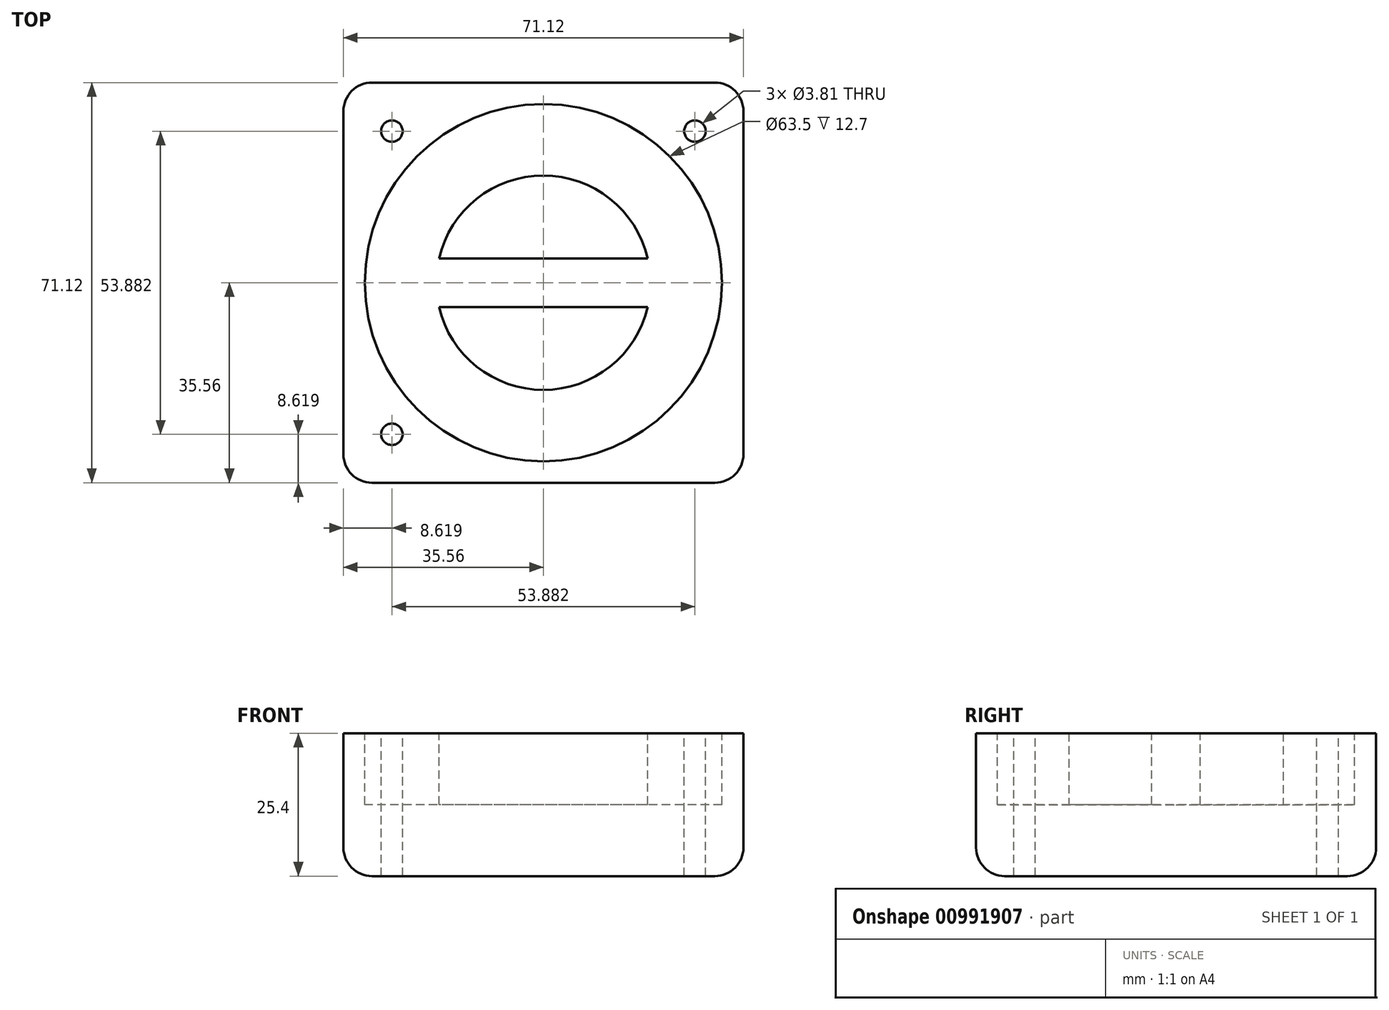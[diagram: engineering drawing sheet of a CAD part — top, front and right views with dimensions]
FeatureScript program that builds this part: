
annotation { "Feature Type Name" : "Feature", "Feature Type Description" : "" }
export const myFeature = defineFeature(function(context is Context, id is Id, definition is map)
    precondition{}
    {
        {
            var Q0;
            Q0=qCreatedBy(makeId("Top.planeOp"),FACE);
            var sketch = newSketch(context, id + "F0", { "sketchPlane" : qUnion([Q0])});
            skLineSegment(sketch, "E0.bottom", {"start": v(35.56, 35.56) * mm, "end": v(-35.56, 35.56) * mm});
            skLineSegment(sketch, "E0.top", {"start": v(35.56, -35.56) * mm, "end": v(-35.56, -35.56) * mm});
            skLineSegment(sketch, "E0.left", {"start": v(35.56, 35.56) * mm, "end": v(35.56, -35.56) * mm});
            skLineSegment(sketch, "E0.right", {"start": v(-35.56, 35.56) * mm, "end": v(-35.56, -35.56) * mm});
            skPoint(sketch, "E0.middle", {"position": v(0, 0) * mm});
            skSolve(sketch);
        }
        {
            var Q0;
            Q0=qSketchRegion(id+"F0",true);
            extrude(context, id + "F1", {"entities" : qUnion([Q0]), "depth" : 25.4 * mm, "offsetDistance" : 25.4 * mm});
        }
        {
            var Q0;
            Q0=makeQuery(id+"F1.opExtrude","CAP_FACE",FACE,{"disambiguationData":[OSD([sQuery(id+"F0.wireOp",EDGE,"E0.bottom"),sQuery(id+"F0.wireOp",EDGE,"E0.top"),sQuery(id+"F0.wireOp",EDGE,"E0.left"),sQuery(id+"F0.wireOp",EDGE,"E0.right")])],"isStart":false});
            var sketch = newSketch(context, id + "F2", { "sketchPlane" : qUnion([Q0])});
            skCircle(sketch, "E1", {"center": v(0, 0) * mm, "radius": 31.75 * mm});
            skSolve(sketch);
        }
        {
            var Q0;
            Q0=qSketchRegion(id+"F2",true);
            extrude(context, id + "F3", {"entities" : qUnion([Q0]), "operationType" : NewBodyOperationType.REMOVE, "oppositeDirection" : true, "depth" : 12.7 * mm, "offsetDistance" : 25.4 * mm});
        }
        {
            var Q0;
            Q0=makeQuery(id+"F3.boolean.opBoolean","COPY",FACE,{"derivedFrom":makeQuery(id+"F3.opExtrude","CAP_FACE",FACE,{"disambiguationData":[OSD([sQuery(id+"F2.wireOp",EDGE,"E1")])],"isStart":false})});
            var sketch = newSketch(context, id + "F4", { "sketchPlane" : qUnion([Q0])});
            skCircle(sketch, "E2", {"center": v(0, 0) * mm, "radius": 19.05 * mm});
            skLineSegment(sketch, "E3.bottom", {"start": v(-64.8, 52.39) * mm, "end": v(68.55, 52.39) * mm, "construction": true});
            skLineSegment(sketch, "E3.top", {"start": v(-64.8, -55.56) * mm, "end": v(68.55, -55.56) * mm, "construction": true});
            skLineSegment(sketch, "E3.left", {"start": v(-64.8, 52.39) * mm, "end": v(-64.8, -55.56) * mm, "construction": true});
            skLineSegment(sketch, "E3.right", {"start": v(68.55, 52.39) * mm, "end": v(68.55, -55.56) * mm, "construction": true});
            skSolve(sketch);
        }
        {
            var Q0;
            Q0=qSketchRegion(id+"F4",true);
            extrude(context, id + "F5", {"entities" : qUnion([Q0]), "operationType" : NewBodyOperationType.ADD, "depth" : 12.7 * mm, "offsetDistance" : 25.4 * mm});
        }
        {
            var Q0;
            Q0=makeQuery(id+"F1.opExtrude","CAP_FACE",FACE,{"disambiguationData":[OSD([sQuery(id+"F0.wireOp",EDGE,"E0.bottom"),sQuery(id+"F0.wireOp",EDGE,"E0.top"),sQuery(id+"F0.wireOp",EDGE,"E0.left"),sQuery(id+"F0.wireOp",EDGE,"E0.right")])],"isStart":false});
            var sketch = newSketch(context, id + "F6", { "sketchPlane" : qUnion([Q0])});
            skCircle(sketch, "E4", {"center": v(-26.94, -26.94) * mm, "radius": 1.9 * mm});
            skCircle(sketch, "E5", {"center": v(-26.94, 26.94) * mm, "radius": 1.9 * mm});
            skPoint(sketch, "E6.middle", {"position": v(0, 0) * mm});
            skLineSegment(sketch, "E7", {"start": v(-26.94, -26.94) * mm, "end": v(0, 0) * mm, "construction": true});
            skLineSegment(sketch, "E8", {"start": v(-26.94, 26.94) * mm, "end": v(0, 0) * mm, "construction": true});
            skLineSegment(sketch, "E9", {"start": v(0, 0) * mm, "end": v(26.94, 26.94) * mm, "construction": true});
            skCircle(sketch, "E10", {"center": v(26.94, 26.94) * mm, "radius": 1.9 * mm});
            skSolve(sketch);
        }
        {
            var Q0;
            Q0=qSketchRegion(id+"F6",true);
            extrude(context, id + "F7", {"entities" : qUnion([Q0]), "operationType" : NewBodyOperationType.REMOVE, "endBound" : BoundingType.THROUGH_ALL, "oppositeDirection" : true, "depth" : 25.4 * mm, "offsetDistance" : 25.4 * mm});
        }
        {
            var Q0;
            Q0=makeQuery(id+"F1.opExtrude","CAP_FACE",FACE,{"disambiguationData":[OSD([sQuery(id+"F0.wireOp",EDGE,"E0.bottom"),sQuery(id+"F0.wireOp",EDGE,"E0.top"),sQuery(id+"F0.wireOp",EDGE,"E0.left"),sQuery(id+"F0.wireOp",EDGE,"E0.right")])],"isStart":false});
            var sketch = newSketch(context, id + "F8", { "sketchPlane" : qUnion([Q0])});
            skLineSegment(sketch, "E11.bottom", {"start": v(18.55, 4.32) * mm, "end": v(-18.55, 4.32) * mm});
            skLineSegment(sketch, "E11.top", {"start": v(18.55, -4.32) * mm, "end": v(-18.55, -4.32) * mm});
            skPoint(sketch, "E11.middle", {"position": v(0, 0) * mm});
            skLineSegment(sketch, "E12", {"start": v(-18.55, 4.32) * mm, "end": v(-18.55, 4.32) * mm});
            skArc(sketch, "E13", {"start": v(18.55, 4.32) * mm, "mid": v(19.05, 0) * mm, "end": v(18.55, -4.32) * mm});
            skArc(sketch, "E14", {"start": v(-18.55, 4.32) * mm, "mid": v(-19.05, 0) * mm, "end": v(-18.55, -4.32) * mm});
            skSolve(sketch);
        }
        {
            var Q0;
            Q0=qSketchRegion(id+"F8",true);
            extrude(context, id + "F9", {"entities" : qUnion([Q0]), "operationType" : NewBodyOperationType.REMOVE, "oppositeDirection" : true, "depth" : 12.7 * mm, "offsetDistance" : 25.4 * mm});
        }
        {
            var Q0;
            Q0=makeQuery(id+"F1.opExtrude","SWEPT_EDGE",EDGE,{"disambiguationData":[OSD([sQuery(id+"F0.wireOp",EDGE,"E0.top"),sQuery(id+"F0.wireOp",EDGE,"E0.right")])]});
            var Q1;
            Q1=makeQuery(id+"F1.opExtrude","CAP_EDGE",EDGE,{"disambiguationData":[OSD([sQuery(id+"F0.wireOp",EDGE,"E0.top")])],"isStart":true});
            var Q2;
            Q2=makeQuery(id+"F1.opExtrude","CAP_EDGE",EDGE,{"disambiguationData":[OSD([sQuery(id+"F0.wireOp",EDGE,"E0.right")])],"isStart":true});
            var Q3;
            Q3=makeQuery(id+"F1.opExtrude","CAP_EDGE",EDGE,{"disambiguationData":[OSD([sQuery(id+"F0.wireOp",EDGE,"E0.bottom")])],"isStart":true});
            var Q4;
            Q4=makeQuery(id+"F1.opExtrude","CAP_EDGE",EDGE,{"disambiguationData":[OSD([sQuery(id+"F0.wireOp",EDGE,"E0.left")])],"isStart":true});
            var Q5;
            Q5=makeQuery(id+"F1.opExtrude","SWEPT_EDGE",EDGE,{"disambiguationData":[OSD([sQuery(id+"F0.wireOp",EDGE,"E0.top"),sQuery(id+"F0.wireOp",EDGE,"E0.left")])]});
            var Q6;
            Q6=makeQuery(id+"F1.opExtrude","SWEPT_EDGE",EDGE,{"disambiguationData":[OSD([sQuery(id+"F0.wireOp",EDGE,"E0.bottom"),sQuery(id+"F0.wireOp",EDGE,"E0.left")])]});
            var Q7;
            Q7=makeQuery(id+"F1.opExtrude","SWEPT_EDGE",EDGE,{"disambiguationData":[OSD([sQuery(id+"F0.wireOp",EDGE,"E0.bottom"),sQuery(id+"F0.wireOp",EDGE,"E0.right")])]});
            fillet(context, id + "F10", {"entities" : qUnion([Q0, Q1, Q2, Q3, Q4, Q5, Q6, Q7]), "radius" : 5.08 * mm, "tangentPropagation" : true, "allowEdgeOverflow" : false});
        }
    });
